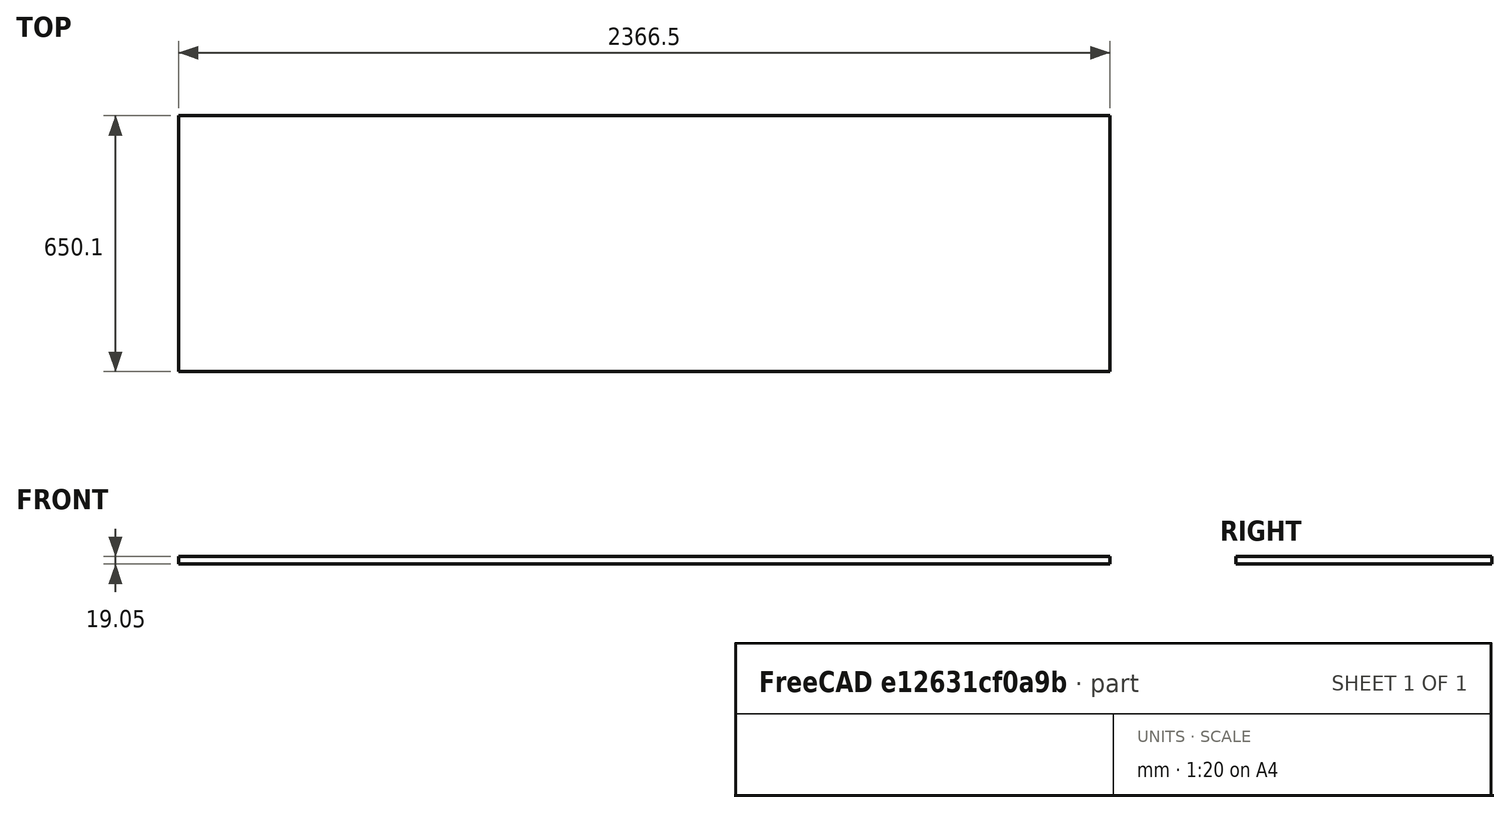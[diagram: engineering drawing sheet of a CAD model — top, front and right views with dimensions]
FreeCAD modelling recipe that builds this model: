
FCSTD DOCUMENT  (FreeCAD 0.20R29177 (Git))
Label: topLeftPlywood
License: All rights reserved
LicenseURL: http://en.wikipedia.org/wiki/All_rights_reserved
objects: Sketcher::SketchObject×1, PartDesign::Pad×1, PartDesign::Body×1
note: 4 computed .brp shape members not serialized (recipe doc carries the construction recipe); baked Part::Feature solids carry a one-line shape summary decoded from their .brp

FEATURE [Sketcher::SketchObject] Sketch
  FullyConstrained = true
  MapMode = 5
  Support = -> [XY_Plane]
  sketch-geometry (4):
    g0: LineSegment StartX=0 StartY=0 StartZ=0 EndX=2366.5 EndY=0 EndZ=0
    g1: LineSegment StartX=2366.5 StartY=0 StartZ=0 EndX=2366.5 EndY=650.1 EndZ=0
    g2: LineSegment StartX=2366.5 StartY=650.1 StartZ=0 EndX=0 EndY=650.1 EndZ=0
    g3: LineSegment StartX=0 StartY=650.1 StartZ=0 EndX=0 EndY=0 EndZ=0
  constraints (11):
    c: Coincident(g0,g1)
    c: Coincident(g1,g2)
    c: Coincident(g2,g3)
    c: Coincident(g3,g0)
    c: Horizontal(g0)
    c: Horizontal(g2)
    c: Vertical(g1)
    c: Vertical(g3)
    c: Coincident(g0,g-1)
    c: DistanceX(g0,g0) = 2366.5
    c: DistanceY(g3,g3) = 650.1
FEATURE [PartDesign::Pad] Pad
  Direction = (0,0,1)
  Length = 19.05
  Length2 = 10
  Profile = -> Sketch
  ReferenceAxis = -> Sketch [N_Axis]
  Type = 0
  expr: Length = 3 / 4 * 25.4
FEATURE [PartDesign::Body] Body
  Group = -> [Sketch,Pad]
  Origin = -> Origin
  Tip = -> Pad
